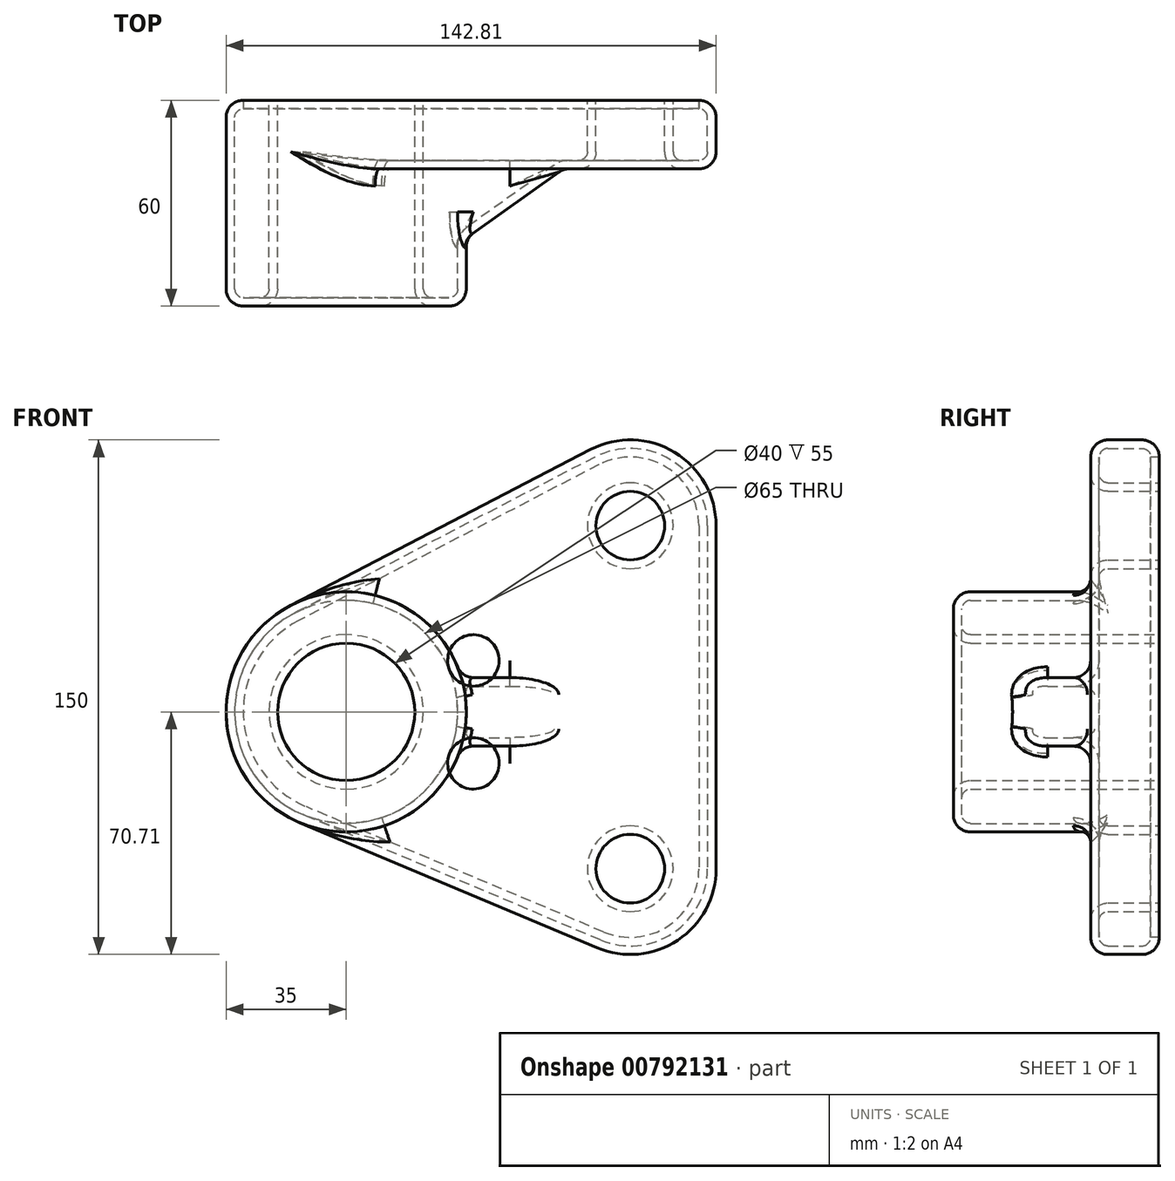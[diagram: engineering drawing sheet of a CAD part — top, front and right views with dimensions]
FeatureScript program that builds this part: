
annotation { "Feature Type Name" : "Feature", "Feature Type Description" : "" }
export const myFeature = defineFeature(function(context is Context, id is Id, definition is map)
    precondition{}
    {
        {
            var Q0;
            Q0=qCreatedBy(makeId("Front.planeOp"),FACE);
            var sketch = newSketch(context, id + "F0", { "sketchPlane" : qUnion([Q0])});
            skCircle(sketch, "E0", {"center": v(0, 0) * mm, "radius": 35 * mm});
            skCircle(sketch, "E1", {"center": v(0, 0) * mm, "radius": 20 * mm});
            skCircle(sketch, "E2", {"center": v(82.8, 54.29) * mm, "radius": 10 * mm});
            skCircle(sketch, "E3", {"center": v(82.8, 54.29) * mm, "radius": 25 * mm});
            skCircle(sketch, "E4", {"center": v(82.8, -45.71) * mm, "radius": 10 * mm});
            skCircle(sketch, "E5", {"center": v(82.8, -45.71) * mm, "radius": 25 * mm});
            skLineSegment(sketch, "E6", {"start": v(71.28, 76.47) * mm, "end": v(-16.14, 31.06) * mm});
            skLineSegment(sketch, "E7", {"start": v(73.1, -68.75) * mm, "end": v(-13.58, -32.26) * mm});
            skLineSegment(sketch, "E8", {"start": v(107.8, 54.29) * mm, "end": v(107.8, -45.71) * mm});
            skSolve(sketch);
        }
        {
            var Q0;
            Q0=makeQuery(id+"F0.imprint","IMPRINT",FACE,{"disambiguationData":[TD([[makeQuery(id+"F0.imprint","IMPRINT",EDGE,{"derivedFrom":sQuery(id+"F0.wireOp",EDGE,"E1")}),-1.0]])]});
            extrude(context, id + "F1", {"entities" : qUnion([Q0]), "depth" : 60 * mm, "offsetDistance" : 25 * mm});
        }
        {
            var Q0;
            Q0=makeQuery(id+"F0.imprint","IMPRINT",FACE,{"disambiguationData":[TD([[makeQuery(id+"F0.imprint","IMPRINT",EDGE,{"derivedFrom":sQuery(id+"F0.wireOp",EDGE,"E2")}),-1.0]])]});
            var Q1;
            {var subQ0=sQuery(id+"F0.wireOp",EDGE,"E6");Q1=makeQuery(id+"F0.imprint","IMPRINT",FACE,{"disambiguationData":[TD([[makeQuery(id+"F0.imprint","IMPRINT",EDGE,{"derivedFrom":subQ0}),1.0]])]});}
            var Q2;
            Q2=makeQuery(id+"F0.imprint","IMPRINT",FACE,{"disambiguationData":[TD([[makeQuery(id+"F0.imprint","IMPRINT",EDGE,{"derivedFrom":sQuery(id+"F0.wireOp",EDGE,"E4")}),-1.0]])]});
            extrude(context, id + "F2", {"entities" : qUnion([Q0, Q1, Q2]), "operationType" : NewBodyOperationType.ADD, "depth" : 20 * mm, "offsetDistance" : 25 * mm});
        }
        {
            var Q0;
            Q0=qCreatedBy(makeId("Top.planeOp"),FACE);
            var sketch = newSketch(context, id + "F3", { "sketchPlane" : qUnion([Q0])});
            skLineSegment(sketch, "E9", {"start": v(26.99, -45.9) * mm, "end": v(68.92, -15.98) * mm});
            skLineSegment(sketch, "E10", {"start": v(26.99, -45.9) * mm, "end": v(26.99, -15.98) * mm});
            skLineSegment(sketch, "E11", {"start": v(26.99, -15.98) * mm, "end": v(68.92, -15.98) * mm});
            skSolve(sketch);
        }
        {
            var Q0;
            Q0 = qSketchRegion(id + "F3", true);
            extrude(context, id + "F4", {"entities" : qUnion([Q0]), "operationType" : NewBodyOperationType.ADD, "endBound" : BoundingType.SYMMETRIC, "depth" : 20 * mm, "offsetDistance" : 25 * mm});
        }
        {
            var Q0;
            Q0=makeQuery(id+"F1.opExtrude","CAP_FACE",FACE,{"disambiguationData":[OSD([sQuery(id+"F0.wireOp",EDGE,"E0"),sQuery(id+"F0.wireOp",EDGE,"E1")])],"isStart":false});
            var Q1;
            Q1=makeQuery(id+"F1.opExtrude","SWEPT_FACE",FACE,{"disambiguationData":[OSD([sQuery(id+"F0.wireOp",EDGE,"E0")])]});
            var Q2;
            Q2=makeQuery(id+"F4.opExtrude","CAP_EDGE",EDGE,{"disambiguationData":[OSD([sQuery(id+"F3.wireOp",EDGE,"E9")])],"isStart":true});
            var Q3;
            Q3=makeQuery(id+"F4.boolean.opBoolean","INTERSECT",EDGE,{"derivedFrom":[makeQuery(id+"F2.opExtrude","CAP_FACE",FACE,{"disambiguationData":[OSD([sQuery(id+"F0.wireOp",EDGE,"E0"),sQuery(id+"F0.wireOp",EDGE,"E2"),sQuery(id+"F0.wireOp",EDGE,"E3"),sQuery(id+"F0.wireOp",EDGE,"E4"),sQuery(id+"F0.wireOp",EDGE,"E5"),sQuery(id+"F0.wireOp",EDGE,"E6"),sQuery(id+"F0.wireOp",EDGE,"E7"),sQuery(id+"F0.wireOp",EDGE,"E8")])],"isStart":false}),makeQuery(id+"F4.opExtrude","CAP_FACE",FACE,{"disambiguationData":[OSD([sQuery(id+"F3.wireOp",EDGE,"E9"),sQuery(id+"F3.wireOp",EDGE,"E10"),sQuery(id+"F3.wireOp",EDGE,"E11")])],"isStart":false})]});
            var Q4;
            Q4=makeQuery(id+"F4.opExtrude","SWEPT_FACE",FACE,{"disambiguationData":[OSD([sQuery(id+"F3.wireOp",EDGE,"E9")])]});
            var Q5;
            Q5=makeQuery(id+"F2.opExtrude","SWEPT_FACE",FACE,{"disambiguationData":[OSD([sQuery(id+"F0.wireOp",EDGE,"E6")])]});
            var Q6;
            Q6=makeQuery(id+"F2.opExtrude","SWEPT_FACE",FACE,{"disambiguationData":[OSD([sQuery(id+"F0.wireOp",EDGE,"E3")])]});
            var Q7;
            Q7=makeQuery(id+"F2.opExtrude","CAP_FACE",FACE,{"disambiguationData":[OSD([sQuery(id+"F0.wireOp",EDGE,"E0"),sQuery(id+"F0.wireOp",EDGE,"E2"),sQuery(id+"F0.wireOp",EDGE,"E3"),sQuery(id+"F0.wireOp",EDGE,"E4"),sQuery(id+"F0.wireOp",EDGE,"E5"),sQuery(id+"F0.wireOp",EDGE,"E6"),sQuery(id+"F0.wireOp",EDGE,"E7"),sQuery(id+"F0.wireOp",EDGE,"E8")])],"isStart":false});
            var Q8;
            Q8=makeQuery(id+"F2.opExtrude","SWEPT_FACE",FACE,{"disambiguationData":[OSD([sQuery(id+"F0.wireOp",EDGE,"E8")])]});
            var Q9;
            Q9=makeQuery(id+"F2.opExtrude","SWEPT_FACE",FACE,{"disambiguationData":[OSD([sQuery(id+"F0.wireOp",EDGE,"E5")])]});
            var Q10;
            Q10=makeQuery(id+"F2.opExtrude","CAP_EDGE",EDGE,{"disambiguationData":[OSD([sQuery(id+"F0.wireOp",EDGE,"E7")])],"isStart":true});
            fillet(context, id + "F5", {"entities" : qUnion([Q0, Q1, Q2, Q3, Q4, Q5, Q6, Q7, Q8, Q9, Q10]), "radius" : 5 * mm, "tangentPropagation" : true, "allowEdgeOverflow" : false});
        }
        {
            var Q0;
            {var subQ0=sQuery(id+"F0.wireOp",EDGE,"E0");Q0=makeQuery(id+"F2.boolean.opBoolean","MERGE",FACE,{"derivedFrom":[makeQuery(id+"F1.opExtrude","CAP_FACE",FACE,{"disambiguationData":[OSD([subQ0,sQuery(id+"F0.wireOp",EDGE,"E1")])],"isStart":true}),makeQuery(id+"F2.opExtrude","CAP_FACE",FACE,{"disambiguationData":[OSD([subQ0,sQuery(id+"F0.wireOp",EDGE,"E2"),sQuery(id+"F0.wireOp",EDGE,"E3"),sQuery(id+"F0.wireOp",EDGE,"E4"),sQuery(id+"F0.wireOp",EDGE,"E5"),sQuery(id+"F0.wireOp",EDGE,"E6"),sQuery(id+"F0.wireOp",EDGE,"E7"),sQuery(id+"F0.wireOp",EDGE,"E8")])],"isStart":true})]});}
            shell(context, id + "F6", {"entities" : qUnion([Q0]), "thickness" : 2.5 * mm});
        }
    });
